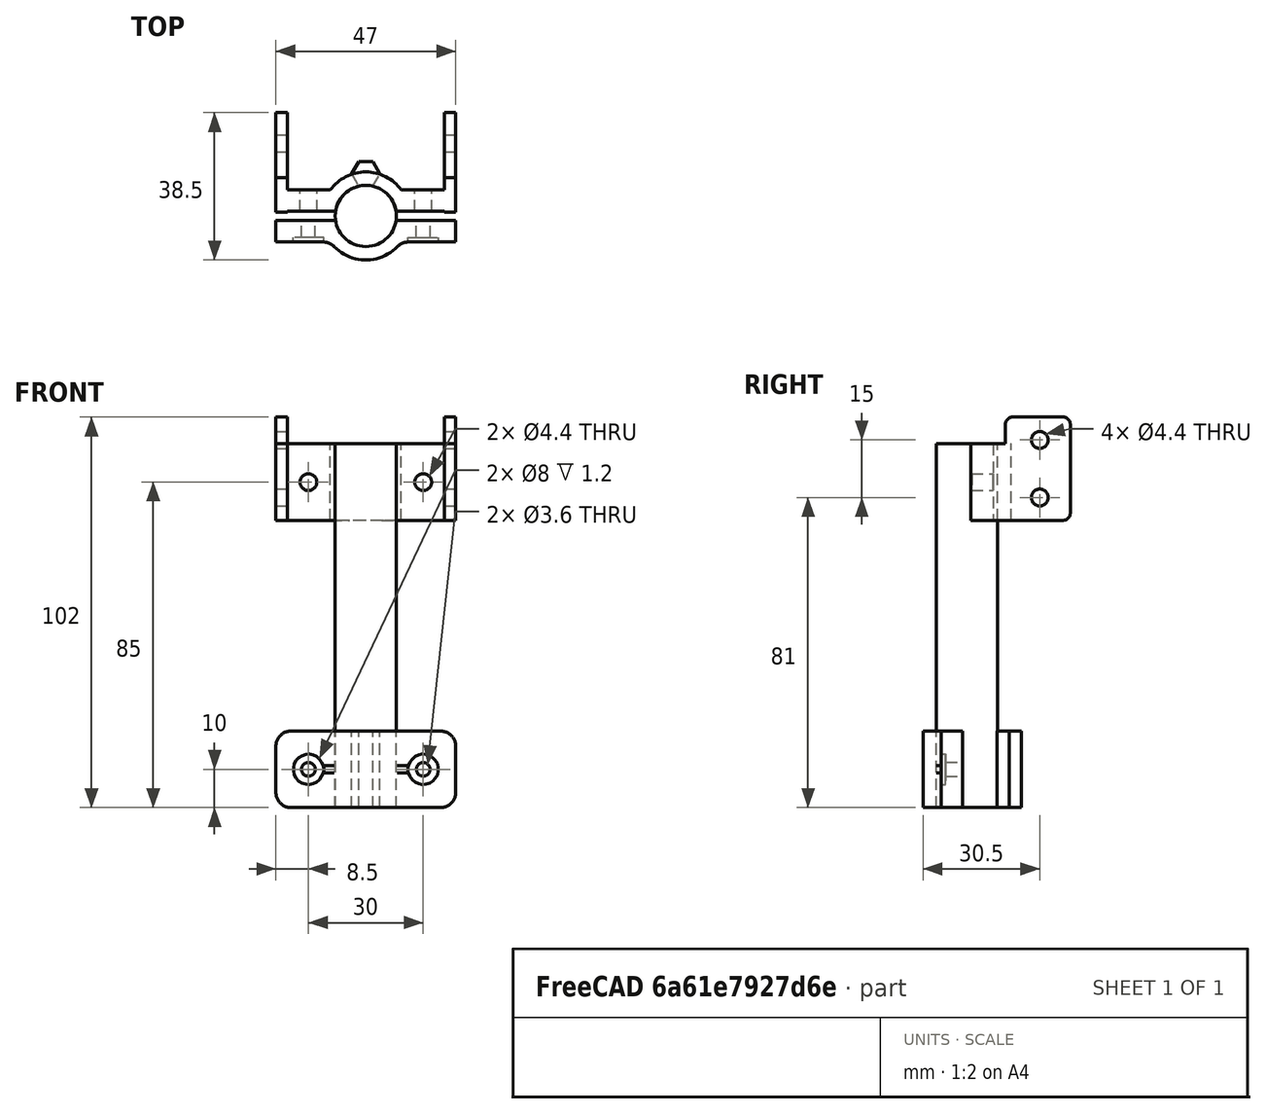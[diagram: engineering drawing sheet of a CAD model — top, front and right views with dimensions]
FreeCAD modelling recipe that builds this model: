
FCSTD DOCUMENT  (FreeCAD 0.19R23578 (Git))
Label: solder_holder
License: All rights reserved
LicenseURL: http://en.wikipedia.org/wiki/All_rights_reserved
objects: Part::Cylinder×8, Part::MultiFuse×7, Part::Cut×4, Part::Mirroring×4, PartDesign::FeatureBase×3, PartDesign::Body×3, Part::Box×3, Part::Extrusion×2, Part::FeaturePython×2, Part::Fillet×2, Spreadsheet::Sheet×1, Part::Feature×1
note: 39 computed .brp shape members not serialized (recipe doc carries the construction recipe); baked Part::Feature solids carry a one-line shape summary decoded from their .brp

FEATURE [Part::Cylinder] Cylinder  label="solder mockup"
  Angle = 360
  AttacherType = Attacher::AttachEngine3D
  Height = 95
  Placement = pos=(0,-11,0) rot=(0,0,1;0rad)
  Radius = 8
FEATURE [Part::Cylinder] Cylinder095  label="bolt head cylinder006"
  Angle = 360
  AttacherType = Attacher::AttachEngine3D
  Height = 20
  Placement = pos=(0,-7.6,4.9e-15) rot=(-1,0,0;1.5708rad)
  Radius = 4
  expr: .Placement.Base.y = 2 - 2 - 2 - <<p>>.bolt_squeeze_wall
FEATURE [Part::Cylinder] Cylinder097  label="pile extraction001"
  Angle = 360
  AttacherType = Attacher::AttachEngine3D
  Height = 20
  Placement = pos=(0,0,0) rot=(0,0,1;0.174533rad)
  Radius = 8
  expr: Radius = <<p>>.pipe_r
FEATURE [Part::Cylinder] Cylinder096  label="outer wall001"
  Angle = 160
  AttacherType = Attacher::AttachEngine3D
  Height = 20
  Placement = pos=(0,0,0) rot=(0,0,1;0.174533rad)
  Radius = 11.5
  expr: Radius = <<p>>.pipe_r + <<p>>.corner_wall
FEATURE [Spreadsheet::Sheet] Spreadsheet  label="p"
  cells = A1=pipe_r; B1(pipe_r)=8; A2=corner_wall; B2(corner_wall)=3.5; A3=cube_wall_sz; B3(cube_wall_sz)==2 * pipe_r + 2 * corner_wall; A4=cube_extra_axis_sz; B4(cube_extra_axis_sz)=20; A5=cube_cut_along_sz; B5(cube_cut_along_sz)=2.4; A6=cube_cut_across_sz; B6(cube_cut_across_sz)=30; A7=bolt_squeeze_wall; B7(bolt_squeeze_wall)=5.6; A8=bolt_squeeze_height; B8(bolt_squeeze_height)=12; A9=cube_profile_width; B9(cube_profile_width)=10; A10=cube_profile_length; B10(cube_profile_length)=20; A11=cube_profile_attachment_height; B11(cube_profile_attachment_height)=40; A12=wall; B12(wall)=3; A13=cube_profile_attachment_length; B13(cube_profile_attachment_length)=16; A14=blocker_circumference; B14(blocker_circumference)==pipe_r * 2 * pi; A15=blocker_r; B15(blocker_r)==pipe_r; A16=insert_hole_r; B16(insert_hole_r)=2.2
FEATURE [Part::Extrusion] Extrude004  label="m3 nut hole001"
  Dir = (0,0,1)
  DirMode = 2
  FaceMakerClass = Part::FaceMakerBullseye
  LengthFwd = 20
  LengthRev = 0
  Solid = true
  Symmetric = false
FEATURE [PartDesign::FeatureBase] Clone036
  BaseFeature = -> Extrude004
FEATURE [PartDesign::Body] Body038  label="m3 nut hole clone004"
  BaseFeature = -> Extrude004
  Group = -> [Clone036]
  Origin = -> Origin061
  Placement = pos=(0,42,0) rot=(1,0,0;1.5708rad)
  Tip = -> Clone036
FEATURE [Part::Box] Box047  label="Cube004"
  AttacherType = Attacher::AttachEngine3D
  Height = 20
  Length = 47
  Placement = pos=(-23.5,1.2,0) rot=(0,0,1;0rad)
  Width = 5.6
  expr: .Placement.Base.y = <<p>>.cube_cut_along_sz / 2
  expr: .Placement.Base.x = -(<<p>>.pipe_r + <<p>>.corner_wall + <<p>>.bolt_squeeze_height)
  expr: Length = (<<p>>.pipe_r + <<p>>.corner_wall + <<p>>.bolt_squeeze_height) * 2
  expr: Width = <<p>>.bolt_squeeze_wall
FEATURE [Part::MultiFuse] Fusion072
  Shapes = -> [Cylinder096,Box047]
FEATURE [Part::Cylinder] Cylinder094  label="m3 bolt hole004"
  Angle = 360
  AttacherType = Attacher::AttachEngine3D
  Height = 30
  Placement = pos=(0,0,0) rot=(-1,0,0;1.5708rad)
  Radius = 1.8
FEATURE [Part::Cut] Cut023016
  Base = -> Fusion072
  Tool = -> Cylinder097
FEATURE [Part::Mirroring] Part__Mirroring005  label="Cut003 (Mirror #2)001"
  Base = (0,2.86102e-06,10)
  Normal = (0,1,-1.19209e-07)
  Source = -> Cut023016
FEATURE [Part::Cylinder] Cylinder098  label="nut cylinder001"
  Angle = 360
  AttacherType = Attacher::AttachEngine3D
  Height = 20
  Placement = pos=(0,25,1.9e-14) rot=(-1,0,0;1.5708rad)
  Radius = 4.5
FEATURE [Part::MultiFuse] Fusion071  label="m3 bolt nut fusion006"
  Shapes = -> [Cylinder094,Body038,Cylinder095,Cylinder098]
FEATURE [PartDesign::FeatureBase] Clone037
  BaseFeature = -> Fusion071
FEATURE [PartDesign::Body] Body039  label="m3 bolt nut fusion clone003"
  BaseFeature = -> Fusion071
  Group = -> [Clone037]
  Origin = -> Origin062
  Placement = pos=(-15,0,10) rot=(0,0,1;0rad)
  Tip = -> Clone037
FEATURE [Part::Mirroring] Part__Mirroring006  label="m3 bolt nut fusion clone002 (Mirror #3)001"
  Base = (9.53674e-07,17.5,10)
  Normal = (1,0,-1.19209e-07)
  Source = -> Body039
FEATURE [Part::MultiFuse] Fusion074  label="m3 bolt nut fusion007"
  Placement = pos=(0,-18,0) rot=(0,0,1;0rad)
  Shapes = -> [Part__Mirroring006,Body039]
FEATURE [Part::Box] Box  label="wall cube"
  AttacherType = Attacher::AttachEngine3D
  Height = 27
  Length = 3
  Width = 17
FEATURE [Part::Cylinder] Cylinder099  label="m4 hole"
  Angle = 360
  AttacherType = Attacher::AttachEngine3D
  Height = 100
  Placement = pos=(-50,9,6) rot=(0,1,0;1.5708rad)
  Radius = 2.2
FEATURE [Part::FeaturePython] Array001  label="m4 hole array"  # Draft array (typed FeaturePython)
  Angle = 360
  ArrayType = 0
  Axis = (0,0,1)
  Base = -> Cylinder099
  Center = (0,0,0)
  Fuse = false
  IntervalAxis = (0,0,0)
  IntervalX = (1,0,0)
  IntervalY = (0,1,0)
  IntervalZ = (0,0,15)
  NumberPolar = 1
  NumberX = 1
  NumberY = 1
  NumberZ = 4
FEATURE [Part::Box] Box048  label="wall cube001"
  AttacherType = Attacher::AttachEngine3D
  Height = 20
  Length = 3
  Placement = pos=(0,-9,0) rot=(0,0,1;0rad)
  Width = 10
FEATURE [Part::MultiFuse] Fusion  label="wall cube fusion"
  Placement = pos=(-23.5,0,0) rot=(0,0,1;0rad)
  Shapes = -> [Box,Box048]
FEATURE [Part::FeaturePython] Array  label="wall cube array"  # Draft array (typed FeaturePython)
  Angle = 360
  ArrayType = 0
  Axis = (0,0,1)
  Base = -> Fusion
  Center = (0,0,0)
  Fuse = false
  IntervalAxis = (0,0,0)
  IntervalX = (44,0,0)
  IntervalY = (0,1,0)
  IntervalZ = (0,0,1)
  NumberPolar = 1
  NumberX = 2
  NumberY = 1
  NumberZ = 1
FEATURE [Part::Cut] Cut  label="walls with holes"
  Base = -> Array
  Placement = pos=(0,10,0) rot=(0,0,1;0rad)
  Tool = -> Array001
FEATURE [Part::MultiFuse] Fusion073
  Shapes = -> [Cut023016,Cut]
FEATURE [Part::Cut] Cut023017  label="mirror cut"
  Base = -> Part__Mirroring005
  Placement = pos=(0,-25,0) rot=(0,0,1;0rad)
  Tool = -> Fusion074
FEATURE [Part::Fillet] Fillet001  label="solder holder outer fillet"
  Base = -> Cut023017
  Edges = 6 edges r=4: [Edge8,Edge21,Edge26,Edge28,Edge48,Edge50]
  Placement = pos=(0,14,0) rot=(0,0,1;0rad)
FEATURE [Part::Feature] z_sliding_block4inserts001001001  label="z_sliding_block4inserts"
  Placement = pos=(-11,42.5,28) rot=(0,0,1;0rad)
  shape: bbox 7 x 27 x 150 mm, 708 faces, 0 solids (baked)
FEATURE [Part::Mirroring] Part__Mirroring  label="z_sliding_block4inserts (Mirror #3)"
  Base = (0,0,0)
  Normal = (1,0,0)
  Source = -> z_sliding_block4inserts001001001
FEATURE [Part::Extrusion] Extrude005  label="m3 nut hole002"
  Dir = (0,0,1)
  DirMode = 2
  FaceMakerClass = Part::FaceMakerBullseye
  LengthFwd = 20
  LengthRev = 0
  Solid = true
  Symmetric = false
FEATURE [Part::Cylinder] Cylinder103  label="insert hole"
  Angle = 360
  AttacherType = Attacher::AttachEngine3D
  Height = 30
  Placement = pos=(15,-19,10) rot=(-1,0,0;1.5708rad)
  Radius = 2.2
  expr: Radius = <<p>>.insert_hole_r
FEATURE [Part::Mirroring] Part__Mirroring007  label="insert (Mirror #4)"
  Base = (0,0,0)
  Normal = (1,0,0)
  Source = -> Cylinder103
FEATURE [Part::MultiFuse] Fusion076  label="m3 bolt insert fusion001"
  Shapes = -> [Part__Mirroring007,Cylinder103]
FEATURE [Part::Cut] Cut023015  label="tube block cut001"
  Base = -> Fusion073
  Placement = pos=(0,-11,0) rot=(0,0,1;0rad)
  Tool = -> Fusion076
FEATURE [Part::Fillet] Fillet  label="solder with walls fillet"
  Base = -> Cut023015
  Edges = 6 edges r=2: [Edge79,Edge104,Edge123,Edge127,Edge144,Edge145]
FEATURE [PartDesign::FeatureBase] Clone
  BaseFeature = -> Fillet
FEATURE [PartDesign::Body] Body  label="solder with walls fillet clone"
  BaseFeature = -> Fillet
  Group = -> [Clone]
  Origin = -> Origin
  Placement = pos=(0,0,75) rot=(0,0,1;0rad)
  Tip = -> Clone
FEATURE [Part::MultiFuse] Fusion077  label="z_sliding_block4insert fusion"
  Shapes = -> [Part__Mirroring,z_sliding_block4inserts001001001]
